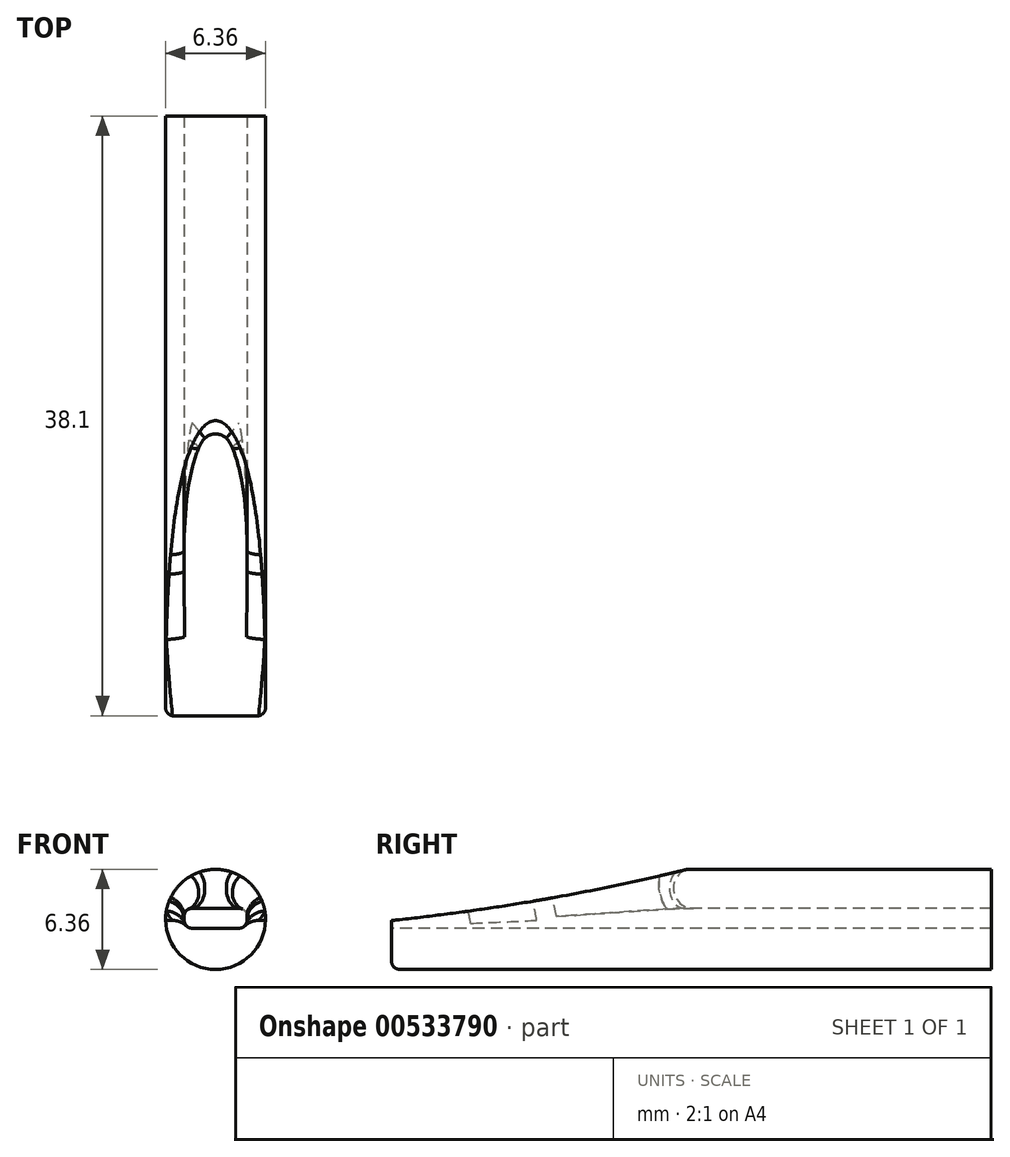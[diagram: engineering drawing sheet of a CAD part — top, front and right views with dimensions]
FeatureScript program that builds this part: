
annotation { "Feature Type Name" : "Feature", "Feature Type Description" : "" }
export const myFeature = defineFeature(function(context is Context, id is Id, definition is map)
    precondition{}
    {
        {
            var Q0;
            Q0=qCreatedBy(makeId("Front.planeOp"),FACE);
            var sketch = newSketch(context, id + "F0", { "sketchPlane" : qUnion([Q0])});
            skCircle(sketch, "E0", {"center": v(0, 0) * mm, "radius": 3.17 * mm});
            skSolve(sketch);
        }
        {
            var Q0;
            Q0=makeQuery(id+"F0.imprint","IMPRINT",FACE,{"disambiguationData":[TD([[makeQuery(id+"F0.imprint","IMPRINT",EDGE,{"derivedFrom":sQuery(id+"F0.wireOp",EDGE,"E0")}),1.0]])]});
            extrude(context, id + "F1", {"entities" : qUnion([Q0]), "depth" : 38.1 * mm, "offsetDistance" : 25.4 * mm});
        }
        {
            var Q0;
            Q0=qCreatedBy(makeId("Right.planeOp"),FACE);
            var sketch = newSketch(context, id + "F2", { "sketchPlane" : qUnion([Q0])});
            skFitSpline(sketch, "E1", {"points": [v(-61.4, 0) * mm, v(-28.65, 1.24) * mm, v(2.6, 11.13) * mm, v(-33.26, 5.74) * mm, v(-61.4, 0) * mm]});
            skSolve(sketch);
        }
        {
            var Q0;
            Q0=qSketchRegion(id+"F2",true);
            extrude(context, id + "F3", {"entities" : qUnion([Q0]), "operationType" : NewBodyOperationType.REMOVE, "endBound" : BoundingType.SYMMETRIC, "oppositeDirection" : true, "depth" : 25.4 * mm, "offsetDistance" : 25.4 * mm});
        }
        {
            var Q0;
            Q0=qCreatedBy(makeId("Front.planeOp"),FACE);
            var sketch = newSketch(context, id + "F4", { "sketchPlane" : qUnion([Q0])});
            skLineSegment(sketch, "E2", {"start": v(0, 4.82) * mm, "end": v(0, -9.2) * mm, "construction": true});
            skLineSegment(sketch, "E3.bottom", {"start": v(0, -0.56) * mm, "end": v(2, -0.56) * mm});
            skLineSegment(sketch, "E3.top", {"start": v(0, 0.7) * mm, "end": v(2, 0.7) * mm});
            skLineSegment(sketch, "E3.left", {"start": v(0, -0.56) * mm, "end": v(0, 0.7) * mm});
            skLineSegment(sketch, "E3.right", {"start": v(2, -0.56) * mm, "end": v(2, 0.7) * mm});
            skLineSegment(sketch, "E4.MirrorCS", {"start": v(0, 0.7) * mm, "end": v(-2, 0.7) * mm});
            skLineSegment(sketch, "E5.MirrorCS", {"start": v(-2, -0.56) * mm, "end": v(-2, 0.7) * mm});
            skLineSegment(sketch, "E6.MirrorCS", {"start": v(0, -0.56) * mm, "end": v(-2, -0.56) * mm});
            skSolve(sketch);
        }
        {
            var Q0;
            Q0=qSketchRegion(id+"F4",true);
            extrude(context, id + "F5", {"entities" : qUnion([Q0]), "operationType" : NewBodyOperationType.REMOVE, "endBound" : BoundingType.SYMMETRIC, "oppositeDirection" : true, "depth" : 76.2 * mm, "offsetDistance" : 25.4 * mm});
        }
        {
            var Q0;
            Q0=makeQuery(id+"F5.boolean.opBoolean","COPY",EDGE,{"derivedFrom":makeQuery(id+"F5.opExtrude","SWEPT_EDGE",EDGE,{"disambiguationData":[OSD([sQuery(id+"F4.wireOp",EDGE,"E5.MirrorCS"),sQuery(id+"F4.wireOp",EDGE,"E6.MirrorCS")])]})});
            var Q1;
            Q1=makeQuery(id+"F5.boolean.opBoolean","COPY",EDGE,{"derivedFrom":makeQuery(id+"F5.opExtrude","SWEPT_EDGE",EDGE,{"disambiguationData":[OSD([sQuery(id+"F4.wireOp",EDGE,"E3.bottom"),sQuery(id+"F4.wireOp",EDGE,"E3.right")])]})});
            var Q2;
            Q2=makeQuery(id+"F5.boolean.opBoolean","COPY",EDGE,{"derivedFrom":makeQuery(id+"F5.opExtrude","SWEPT_EDGE",EDGE,{"disambiguationData":[OSD([sQuery(id+"F4.wireOp",EDGE,"E3.top"),sQuery(id+"F4.wireOp",EDGE,"E3.right")])]})});
            var Q3;
            Q3=makeQuery(id+"F5.boolean.opBoolean","COPY",EDGE,{"derivedFrom":makeQuery(id+"F5.opExtrude","SWEPT_EDGE",EDGE,{"disambiguationData":[OSD([sQuery(id+"F4.wireOp",EDGE,"E4.MirrorCS"),sQuery(id+"F4.wireOp",EDGE,"E5.MirrorCS")])]})});
            fillet(context, id + "F6", {"entities" : qUnion([Q0, Q1, Q2, Q3]), "radius" : 0.5 * mm, "tangentPropagation" : true, "allowEdgeOverflow" : false});
        }
        {
            var Q0;
            Q0=makeQuery(id+"F1.opExtrude","CAP_EDGE",EDGE,{"disambiguationData":[OSD([sQuery(id+"F0.wireOp",EDGE,"E0")])],"isStart":false});
            fillet(context, id + "F7", {"entities" : qUnion([Q0]), "radius" : 0.5 * mm, "tangentPropagation" : true, "allowEdgeOverflow" : false});
        }
        {
            var Q0;
            Q0=makeQuery(id+"F5.boolean.opBoolean","INTERSECT",EDGE,{"derivedFrom":[makeQuery(id+"F3.boolean.opBoolean","COPY",FACE,{"derivedFrom":makeQuery(id+"F3.opExtrude","SWEPT_FACE",FACE,{"disambiguationData":[OSD([sQuery(id+"F2.wireOp",EDGE,"E1")])]})}),makeQuery(id+"F5.opExtrude","SWEPT_FACE",FACE,{"disambiguationData":[OSD([sQuery(id+"F4.wireOp",EDGE,"E3.top"),sQuery(id+"F4.wireOp",EDGE,"E4.MirrorCS")])]})]});
            fillet(context, id + "F8", {"entities" : qUnion([Q0]), "radius" : 1.27 * mm, "tangentPropagation" : true, "allowEdgeOverflow" : false});
        }
    });
